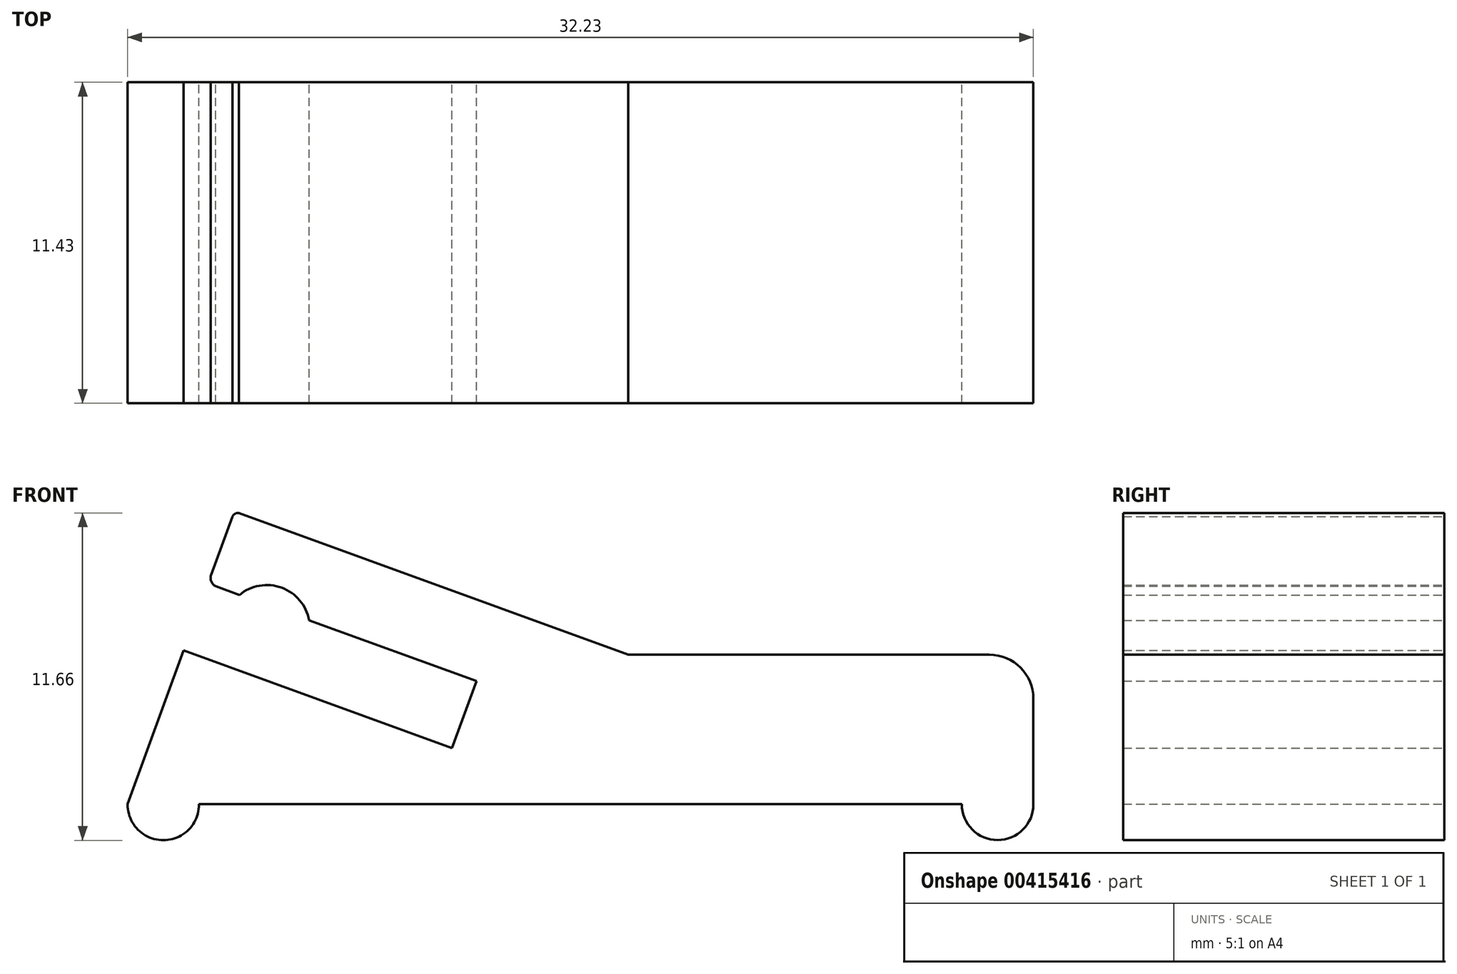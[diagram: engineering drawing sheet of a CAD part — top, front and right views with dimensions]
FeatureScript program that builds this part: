
annotation { "Feature Type Name" : "Feature", "Feature Type Description" : "" }
export const myFeature = defineFeature(function(context is Context, id is Id, definition is map)
    precondition{}
    {
        {
            var Q0;
            Q0=qCreatedBy(makeId("Front.planeOp"),FACE);
            var sketch = newSketch(context, id + "F0", { "sketchPlane" : qUnion([Q0])});
            skLineSegment(sketch, "E0.top", {"start": v(-5.61, -10.37) * mm, "end": v(7.23, -10.37) * mm});
            skLineSegment(sketch, "E0.left", {"start": v(-23.43, -15.7) * mm, "end": v(-21.44, -10.22) * mm});
            skLineSegment(sketch, "E0.right", {"start": v(8.8, -15.7) * mm, "end": v(8.8, -11.94) * mm});
            skLineSegment(sketch, "E1.bottom", {"start": v(-20.9, -15.7) * mm, "end": v(6.25, -15.7) * mm});
            skPoint(sketch, "E0.bottom.start.orphan", {"position": v(-23.43, -15.7) * mm});
            skArc(sketch, "E2", {"start": v(-23.43, -15.7) * mm, "mid": v(-22.16, -16.98) * mm, "end": v(-20.9, -15.7) * mm});
            skArc(sketch, "E3", {"start": v(6.25, -15.7) * mm, "mid": v(7.53, -16.97) * mm, "end": v(8.8, -15.7) * mm});
            skArc(sketch, "E4.filletArc", {"start": v(8.8, -11.94) * mm, "mid": v(8.34, -10.83) * mm, "end": v(7.23, -10.37) * mm});
            skLineSegment(sketch, "E5.bottom", {"start": v(-20.3, -7.94) * mm, "end": v(-19.45, -8.24) * mm});
            skLineSegment(sketch, "E5.top", {"start": v(-21.44, -10.22) * mm, "end": v(-11.89, -13.7) * mm});
            skLineSegment(sketch, "E5.right", {"start": v(-11.02, -11.31) * mm, "end": v(-11.89, -13.7) * mm});
            skLineSegment(sketch, "E6.trimOffspring", {"start": v(-20.46, -7.53) * mm, "end": v(-19.7, -5.46) * mm});
            skArc(sketch, "E7", {"start": v(-16.97, -9.14) * mm, "mid": v(-17.95, -7.98) * mm, "end": v(-19.45, -8.24) * mm});
            skArc(sketch, "E8", {"start": v(-20.46, -7.53) * mm, "mid": v(-20.45, -7.8) * mm, "end": v(-20.25, -7.95) * mm});
            skLineSegment(sketch, "E9.trimOffspring", {"start": v(-16.97, -9.14) * mm, "end": v(-11.02, -11.31) * mm});
            skLineSegment(sketch, "E10", {"start": v(-19.47, -5.32) * mm, "end": v(-5.61, -10.37) * mm});
            skArc(sketch, "E11", {"start": v(-19.37, -5.36) * mm, "mid": v(-19.58, -5.34) * mm, "end": v(-19.72, -5.49) * mm});
            skSolve(sketch);
        }
        {
            var Q0;
            Q0=makeQuery(id+"F0.imprint","IMPRINT",FACE,{"disambiguationData":[TD([[makeQuery(id+"F0.imprint","IMPRINT",EDGE,{"derivedFrom":sQuery(id+"F0.wireOp",EDGE,"E0.top")}),-1.0]])]});
            extrude(context, id + "F1", {"entities" : qUnion([Q0]), "depth" : 11.43 * mm});
        }
    });
